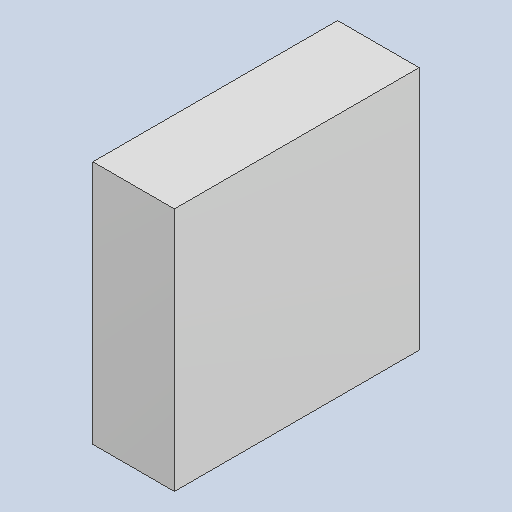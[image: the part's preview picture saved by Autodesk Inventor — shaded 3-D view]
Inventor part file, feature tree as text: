
AUTODESK INVENTOR PART (.ipt)
format: ipt  version: 2023.4 (Build 274418000, 418)  size: 81,408 bytes
history: native  units: mm
features: extrude x1
ambient origin geometry x8: Origin, YZ Plane, XZ Plane, XY Plane, X Axis, Y Axis, Z Axis, Center Point
bodies: Solid1 (feature_tree)
feature tree (1):
  extrude  "Extruded_44"  [1 undecoded]
note: 1 required parameter value undecoded (feature->parameter linkage not recoverable at this tier; creation-order binding heuristic only, values carry confidence <= 0.55)
